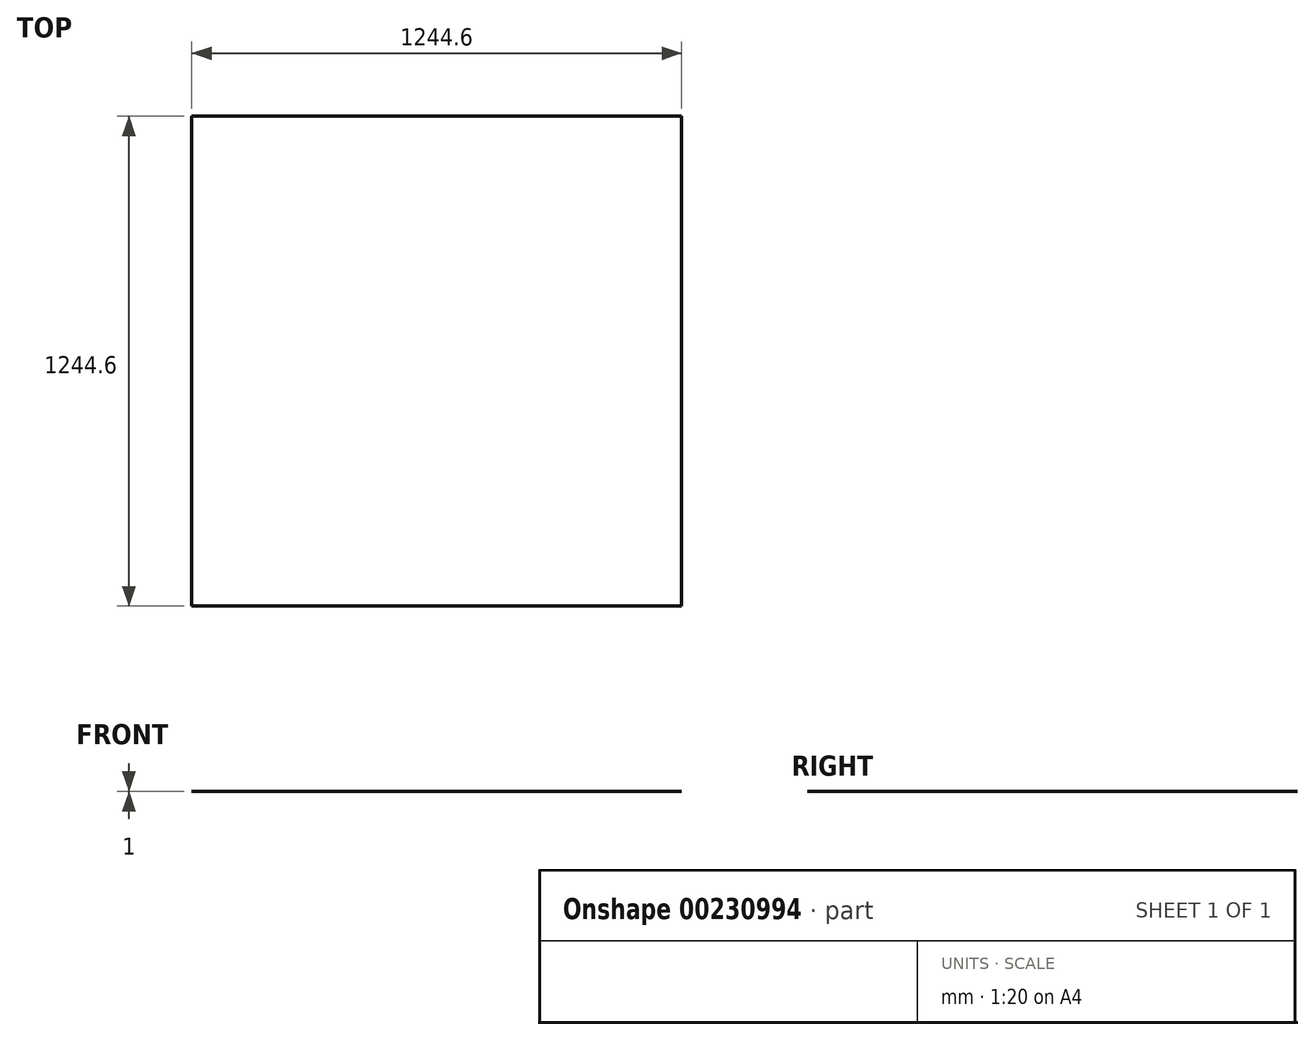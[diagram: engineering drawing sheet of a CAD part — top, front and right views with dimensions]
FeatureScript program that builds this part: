
annotation { "Feature Type Name" : "Feature", "Feature Type Description" : "" }
export const myFeature = defineFeature(function(context is Context, id is Id, definition is map)
    precondition{}
    {
        {
            var Q0;
            Q0=qCreatedBy(makeId("Top.planeOp"),FACE);
            var sketch = newSketch(context, id + "F0", { "sketchPlane" : qUnion([Q0])});
            skLineSegment(sketch, "E0.bottom", {"start": v(-622.3, -622.3) * mm, "end": v(622.3, -622.3) * mm});
            skLineSegment(sketch, "E0.top", {"start": v(-622.3, 622.3) * mm, "end": v(622.3, 622.3) * mm});
            skLineSegment(sketch, "E0.left", {"start": v(-622.3, -622.3) * mm, "end": v(-622.3, 622.3) * mm});
            skLineSegment(sketch, "E0.right", {"start": v(622.3, -622.3) * mm, "end": v(622.3, 622.3) * mm});
            skPoint(sketch, "E0.middle", {"position": v(0, 0) * mm});
            skSolve(sketch);
        }
        {
            var Q0;
            Q0=makeQuery(id+"F0.imprint","IMPRINT",FACE,{"disambiguationData":[TD([[makeQuery(id+"F0.imprint","IMPRINT",EDGE,{"derivedFrom":sQuery(id+"F0.wireOp",EDGE,"E0.bottom")}),1.0]])]});
            extrude(context, id + "F1", {"entities" : qUnion([Q0]), "depth" : 1 * mm});
        }
    });
